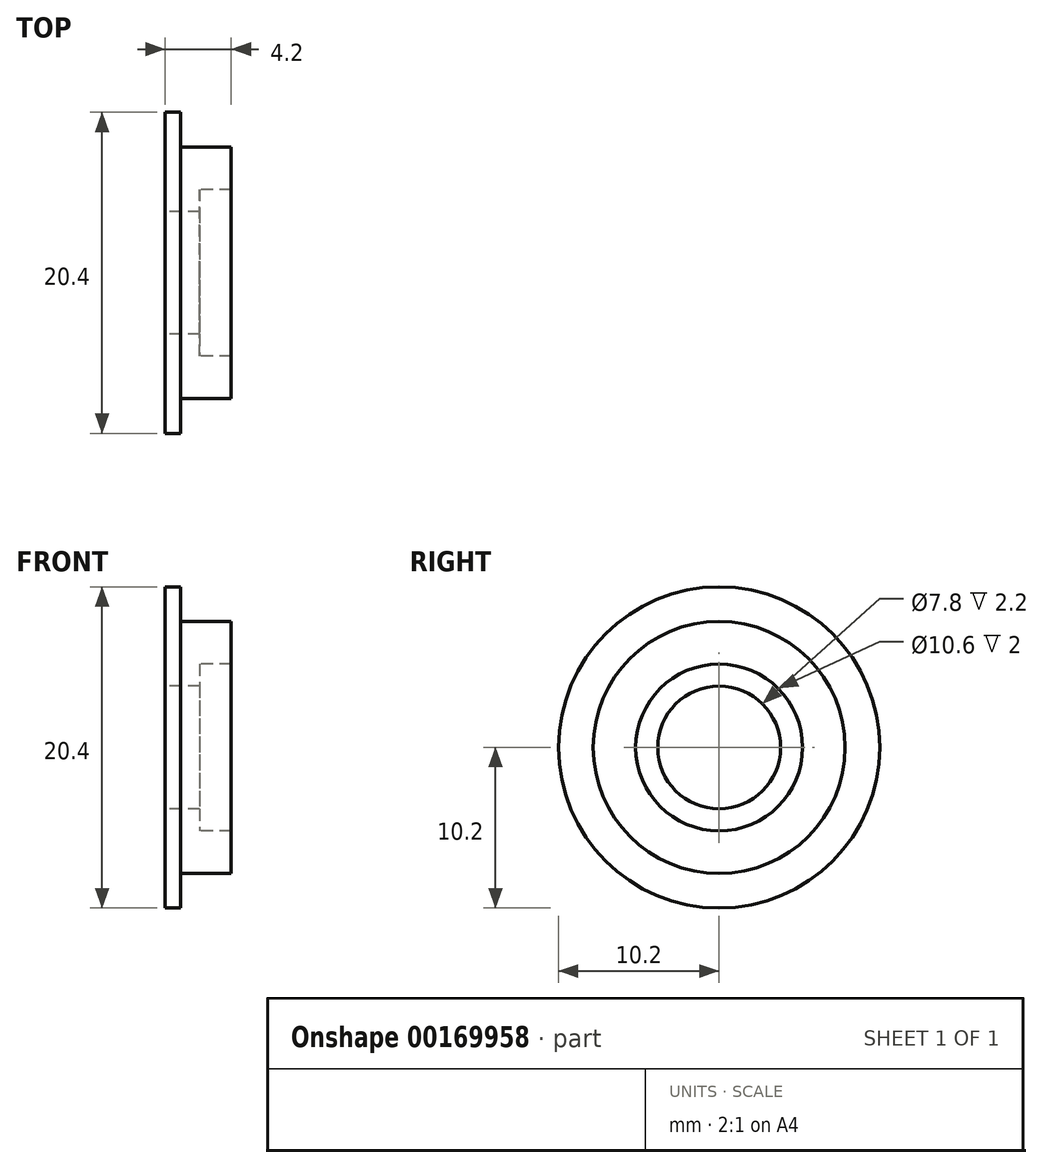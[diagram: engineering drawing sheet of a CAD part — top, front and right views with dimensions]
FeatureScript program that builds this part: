
annotation { "Feature Type Name" : "Feature", "Feature Type Description" : "" }
export const myFeature = defineFeature(function(context is Context, id is Id, definition is map)
    precondition{}
    {
        {
            var Q0;
            Q0=qCreatedBy(makeId("Front.planeOp"),FACE);
            var sketch = newSketch(context, id + "F0", { "sketchPlane" : qUnion([Q0])});
            skLineSegment(sketch, "E0", {"start": v(0, 3.9) * mm, "end": v(0, 10.2) * mm});
            skLineSegment(sketch, "E1", {"start": v(0, 10.2) * mm, "end": v(1, 10.2) * mm});
            skLineSegment(sketch, "E2", {"start": v(1, 10.2) * mm, "end": v(1, 8) * mm});
            skLineSegment(sketch, "E3", {"start": v(1, 8) * mm, "end": v(4.2, 8) * mm});
            skLineSegment(sketch, "E4", {"start": v(4.2, 8) * mm, "end": v(4.2, 5.3) * mm});
            skLineSegment(sketch, "E5", {"start": v(4.2, 5.3) * mm, "end": v(2.2, 5.3) * mm});
            skLineSegment(sketch, "E6", {"start": v(2.2, 5.3) * mm, "end": v(2.2, 3.9) * mm});
            skLineSegment(sketch, "E7", {"start": v(0, 3.9) * mm, "end": v(2.2, 3.9) * mm});
            skLineSegment(sketch, "E8", {"start": v(0, 0) * mm, "end": v(2.2, 0) * mm, "construction": true});
            skSolve(sketch);
        }
        {
            var Q0;
            Q0 = qSketchRegion(id + "F0", true);
            var Q1;
            Q1=sQuery(id+"F0.wireOp",EDGE,"E8");
            revolve(context, id + "F1", {"entities" : qUnion([Q0]), "axis" : qUnion([Q1]), "revolveType" : RevolveType.FULL});
        }
    });
